# Revit family: Faucet-Bidet-American_Standard-Serin-2064.011.rfacccc
name_source: partatom
category: Plumbing Fixtures
units: mm (PartAtom-declared; Revit-internal decimal feet)

## family parameters
Always vertical = No
Cut with Voids When Loaded = Yes
OmniClass Number = 23.45.55.14
OmniClass Title = Single Faucets
Part Type = Normal
Room Calculation Point = No
Round Connector Dimension = Use Diameter
Shared = Yes
Work Plane-Based = Yes

## types (1)
- 2064.011.002
    ADA Compliant = Yes
    ANSI A117.1 = Yes
    ASME A112.18.1/CSA B125.1 = Yes
    Assembly Code = D2020300
    CW Connection = No
    CWFU = 1.5
    Default Elevation = 0"
    Description = Serin® Monoblock Bidet Fitting
    Diameter = 2"
    Finish = Brass-American Standard-002-Polished Chrome
    HW Connection = No
    HWFU = 1.5
    Height = 6 3/8"
    Installation Type = Deck Mounted
    Length = 4 3/8"
    Manufacturer = American Standard
    Material = Brass-American Standard-002-Polished Chrome
    Model = 2064.011.002
    Pop-up Drain Depth = 3"
    Pop-up Drain Included = Yes
    Pop-up Drain Width from Faucet Centre = 4"
    Price = Prices may vary. Please consult Manufacturer Representative for most up-to-date price list.
    Product Documentation Link = https://americanstandard.box.com
    Product Page URL = https://www.americanstandard-us.com
    Revised Date = 07/25/2022
    Tempered Water Connection = Yes
    Tempered Water Connection Diameter = 3/8"
    URL = http://www.americanstandard-us.com
    Vent Connection = No
    WFU = 2
    Waste Connection = No

## geometry (parser evidence)
native form markers: Sweep x2
no freeform markers — native parametric forms only
